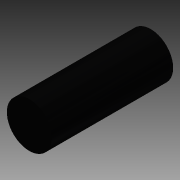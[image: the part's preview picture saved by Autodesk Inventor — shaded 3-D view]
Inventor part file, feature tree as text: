
AUTODESK INVENTOR PART (.ipt)
format: ipt  version: 2014 SP1 (Build 180222100, 222)  size: 69,632 bytes
history: native  units: in
note: dims shown in document units (in); Inventor stores cm internally (conversion verified against a paired STEP export)
features: extrude x1, sketch x1
ambient origin geometry x8: Origin, YZ Plane, XZ Plane, XY Plane, X Axis, Y Axis, Z Axis, Center Point
bodies: Solid1 (feature_tree)
feature tree (2):
  extrude  "Extrusion1"  Depth=0.2362in TaperAngle=0.0deg
  sketch  "Sketch1"  dims[d0=0.0871in d2=0.2362in d3=0.0in]
